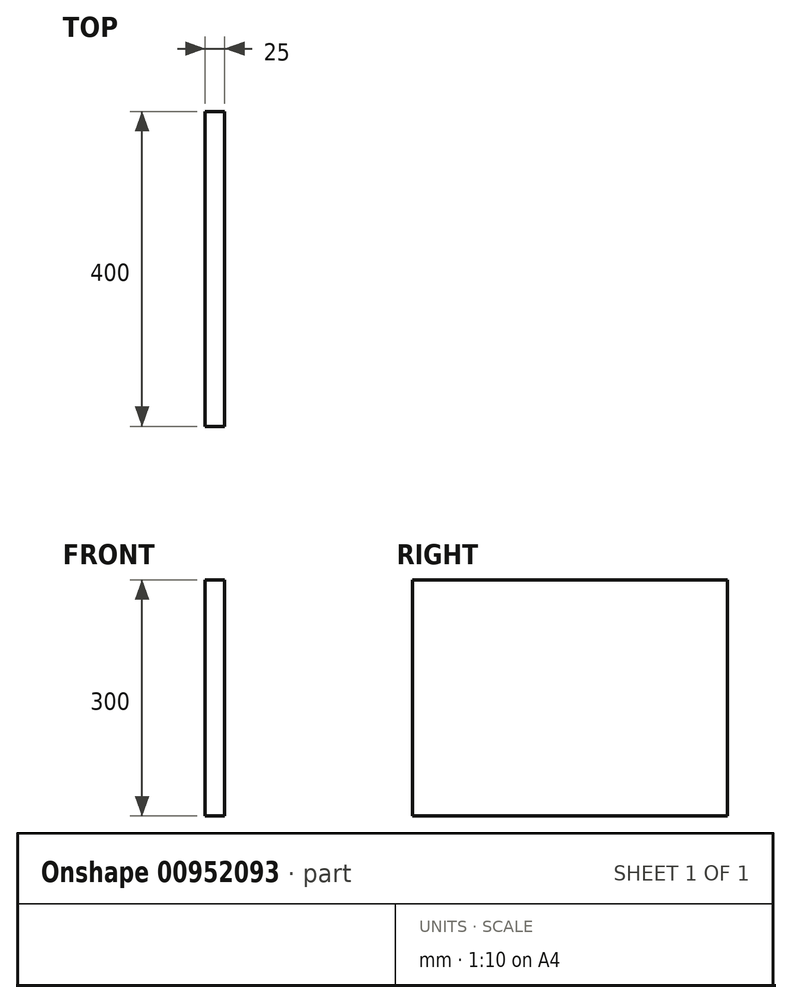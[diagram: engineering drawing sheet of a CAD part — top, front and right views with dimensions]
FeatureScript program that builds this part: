
annotation { "Feature Type Name" : "Feature", "Feature Type Description" : "" }
export const myFeature = defineFeature(function(context is Context, id is Id, definition is map)
    precondition{}
    {
        {
            var Q0;
            Q0=qCreatedBy(makeId("Right.planeOp"),FACE);
            var sketch = newSketch(context, id + "F0", { "sketchPlane" : qUnion([Q0])});
            skLineSegment(sketch, "E0.bottom", {"start": v(200, 150) * mm, "end": v(-200, 150) * mm});
            skLineSegment(sketch, "E0.top", {"start": v(200, -150) * mm, "end": v(-200, -150) * mm});
            skLineSegment(sketch, "E0.left", {"start": v(200, 150) * mm, "end": v(200, -150) * mm});
            skLineSegment(sketch, "E0.right", {"start": v(-200, 150) * mm, "end": v(-200, -150) * mm});
            skPoint(sketch, "E0.middle", {"position": v(0, 0) * mm});
            skSolve(sketch);
        }
        {
            var Q0;
            Q0=makeQuery(id+"F0.imprint","IMPRINT",FACE,{"disambiguationData":[TD([[makeQuery(id+"F0.imprint","IMPRINT",EDGE,{"derivedFrom":sQuery(id+"F0.wireOp",EDGE,"E0.bottom")}),1.0]])]});
            extrude(context, id + "F1", {"entities" : qUnion([Q0]), "depth" : 25 * mm, "offsetDistance" : 25 * mm});
        }
    });
